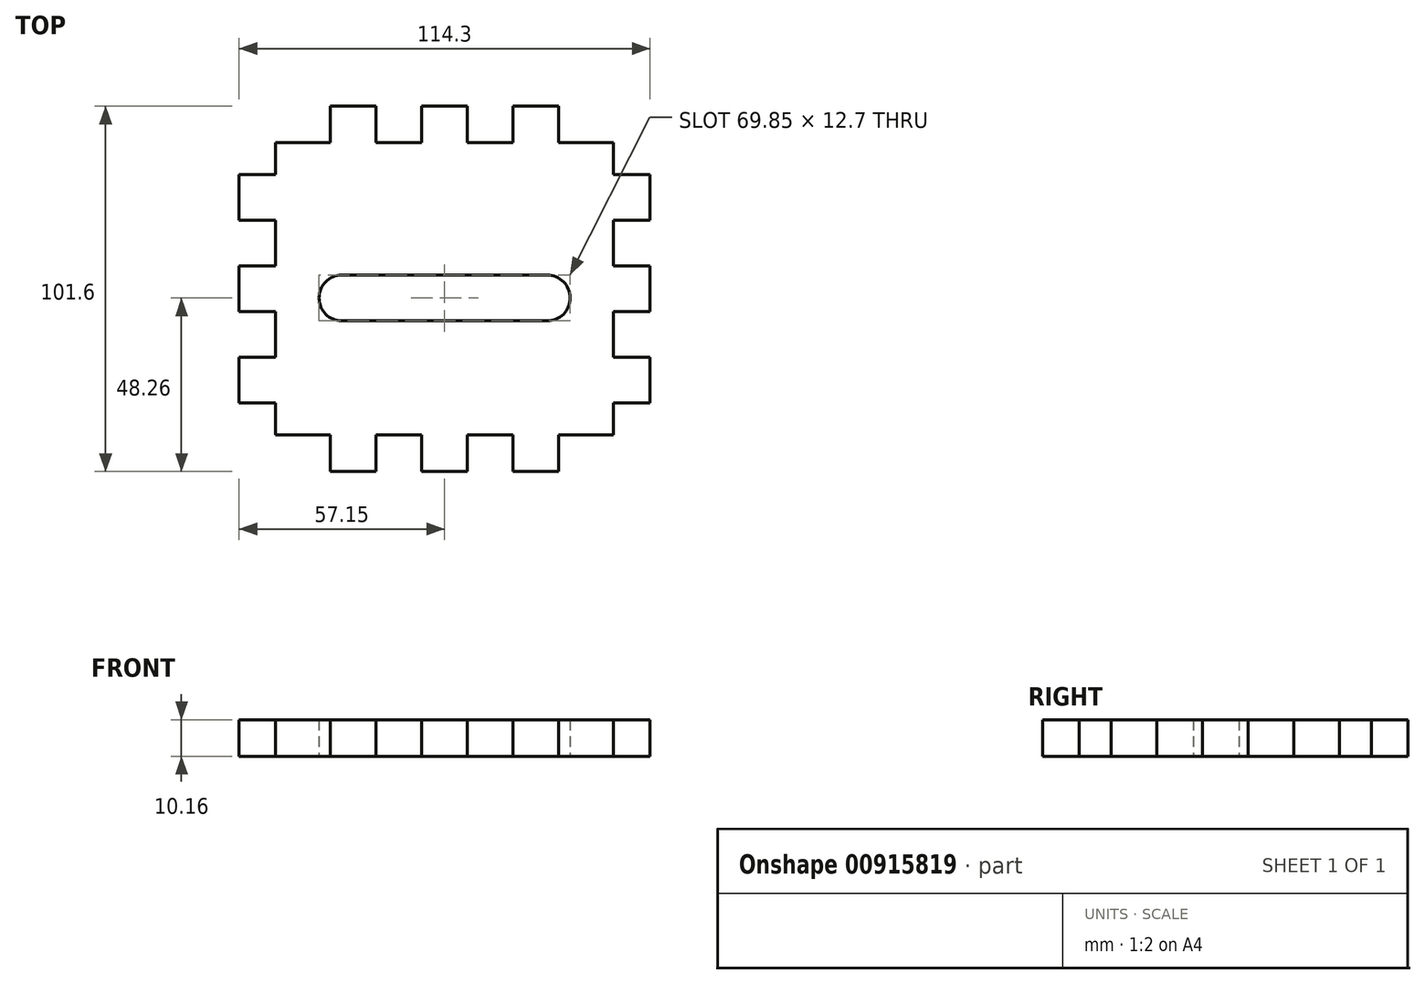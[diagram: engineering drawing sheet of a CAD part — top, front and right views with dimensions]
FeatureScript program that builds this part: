
annotation { "Feature Type Name" : "Feature", "Feature Type Description" : "" }
export const myFeature = defineFeature(function(context is Context, id is Id, definition is map)
    precondition{}
    {
        {
            var Q0;
            Q0=qCreatedBy(makeId("Top.planeOp"),FACE);
            var sketch = newSketch(context, id + "F0", { "sketchPlane" : qUnion([Q0])});
            skLineSegment(sketch, "E0.bottom", {"start": v(25.4, 0) * mm, "end": v(38.1, 0) * mm});
            skLineSegment(sketch, "E0.left", {"start": v(0, -19.05) * mm, "end": v(0, -31.75) * mm});
            skLineSegment(sketch, "E1", {"start": v(10.16, -10.16) * mm, "end": v(25.4, -10.16) * mm});
            skLineSegment(sketch, "E2", {"start": v(25.4, -10.16) * mm, "end": v(25.4, 0) * mm});
            skPoint(sketch, "E3.orphan", {"position": v(0, 0) * mm});
            skLineSegment(sketch, "E4", {"start": v(38.1, 0) * mm, "end": v(38.1, -10.16) * mm});
            skLineSegment(sketch, "E5", {"start": v(38.1, -10.16) * mm, "end": v(50.8, -10.16) * mm});
            skLineSegment(sketch, "E6", {"start": v(50.8, -10.16) * mm, "end": v(50.8, 0) * mm});
            skLineSegment(sketch, "E7", {"start": v(50.8, 0) * mm, "end": v(63.5, 0) * mm});
            skLineSegment(sketch, "E8", {"start": v(63.5, 0) * mm, "end": v(63.5, -10.16) * mm});
            skLineSegment(sketch, "E9", {"start": v(63.5, -10.16) * mm, "end": v(76.2, -10.16) * mm});
            skLineSegment(sketch, "E10", {"start": v(76.2, -10.16) * mm, "end": v(76.2, 0) * mm});
            skLineSegment(sketch, "E11.trimOffspring", {"start": v(76.2, 0) * mm, "end": v(88.9, 0) * mm});
            skLineSegment(sketch, "E12", {"start": v(88.9, 0) * mm, "end": v(88.9, -10.16) * mm});
            skLineSegment(sketch, "E13", {"start": v(88.9, -10.16) * mm, "end": v(104.14, -10.16) * mm});
            skPoint(sketch, "E14.orphan", {"position": v(114.3, 0) * mm});
            skLineSegment(sketch, "E15", {"start": v(10.16, -10.16) * mm, "end": v(10.16, -19.05) * mm});
            skLineSegment(sketch, "E16", {"start": v(10.16, -19.05) * mm, "end": v(0, -19.05) * mm});
            skLineSegment(sketch, "E17", {"start": v(0, -31.75) * mm, "end": v(10.16, -31.75) * mm});
            skLineSegment(sketch, "E18", {"start": v(10.16, -31.75) * mm, "end": v(10.16, -44.45) * mm});
            skLineSegment(sketch, "E19", {"start": v(10.16, -44.45) * mm, "end": v(0, -44.45) * mm});
            skLineSegment(sketch, "E20", {"start": v(0, -44.45) * mm, "end": v(0, -57.15) * mm});
            skLineSegment(sketch, "E21", {"start": v(0, -57.15) * mm, "end": v(10.16, -57.15) * mm});
            skLineSegment(sketch, "E22", {"start": v(10.16, -57.15) * mm, "end": v(10.16, -69.85) * mm});
            skLineSegment(sketch, "E23", {"start": v(10.16, -69.85) * mm, "end": v(0, -69.85) * mm});
            skLineSegment(sketch, "E24.trimOffspring", {"start": v(0, -69.85) * mm, "end": v(0, -82.55) * mm});
            skLineSegment(sketch, "E25", {"start": v(0, -82.55) * mm, "end": v(10.16, -82.55) * mm});
            skLineSegment(sketch, "E26", {"start": v(10.16, -82.55) * mm, "end": v(10.16, -91.44) * mm});
            skLineSegment(sketch, "E27", {"start": v(10.16, -91.44) * mm, "end": v(25.4, -91.44) * mm});
            skLineSegment(sketch, "E28", {"start": v(25.4, -91.44) * mm, "end": v(25.4, -101.6) * mm});
            skPoint(sketch, "E29.orphan", {"position": v(0, -101.6) * mm});
            skLineSegment(sketch, "E30", {"start": v(57.15, 0) * mm, "end": v(57.15, 0) * mm});
            skLineSegment(sketch, "E31", {"start": v(0, -50.8) * mm, "end": v(0, -50.8) * mm});
            skLineSegment(sketch, "E32.MirrorCS", {"start": v(104.14, -10.16) * mm, "end": v(104.14, -19.05) * mm});
            skLineSegment(sketch, "E33.MirrorCS", {"start": v(104.14, -19.05) * mm, "end": v(114.3, -19.05) * mm});
            skLineSegment(sketch, "E34.MirrorCS", {"start": v(114.3, -19.05) * mm, "end": v(114.3, -31.75) * mm});
            skLineSegment(sketch, "E35.MirrorCS", {"start": v(114.3, -31.75) * mm, "end": v(104.14, -31.75) * mm});
            skLineSegment(sketch, "E36.MirrorCS", {"start": v(104.14, -31.75) * mm, "end": v(104.14, -44.45) * mm});
            skLineSegment(sketch, "E37.MirrorCS", {"start": v(104.14, -44.45) * mm, "end": v(114.3, -44.45) * mm});
            skLineSegment(sketch, "E38.MirrorCS", {"start": v(114.3, -44.45) * mm, "end": v(114.3, -57.15) * mm});
            skLineSegment(sketch, "E39.MirrorCS", {"start": v(114.3, -57.15) * mm, "end": v(104.14, -57.15) * mm});
            skLineSegment(sketch, "E40.MirrorCS", {"start": v(104.14, -57.15) * mm, "end": v(104.14, -69.85) * mm});
            skLineSegment(sketch, "E41.MirrorCS", {"start": v(104.14, -69.85) * mm, "end": v(114.3, -69.85) * mm});
            skLineSegment(sketch, "E42.MirrorCS", {"start": v(114.3, -69.85) * mm, "end": v(114.3, -82.55) * mm});
            skLineSegment(sketch, "E43.MirrorCS", {"start": v(114.3, -82.55) * mm, "end": v(104.14, -82.55) * mm});
            skLineSegment(sketch, "E44.MirrorCS", {"start": v(104.14, -82.55) * mm, "end": v(104.14, -91.44) * mm});
            skLineSegment(sketch, "E45.MirrorCS", {"start": v(104.14, -91.44) * mm, "end": v(88.9, -91.44) * mm});
            skLineSegment(sketch, "E46.MirrorCS", {"start": v(88.9, -91.44) * mm, "end": v(88.9, -101.6) * mm});
            skLineSegment(sketch, "E47.MirrorCS", {"start": v(25.4, -101.6) * mm, "end": v(38.1, -101.6) * mm});
            skLineSegment(sketch, "E48.MirrorCS", {"start": v(38.1, -101.6) * mm, "end": v(38.1, -91.44) * mm});
            skLineSegment(sketch, "E49.MirrorCS", {"start": v(38.1, -91.44) * mm, "end": v(50.8, -91.44) * mm});
            skLineSegment(sketch, "E50.MirrorCS", {"start": v(50.8, -91.44) * mm, "end": v(50.8, -101.6) * mm});
            skLineSegment(sketch, "E51.MirrorCS", {"start": v(63.5, -101.6) * mm, "end": v(63.5, -91.44) * mm});
            skLineSegment(sketch, "E52.MirrorCS", {"start": v(63.5, -91.44) * mm, "end": v(76.2, -91.44) * mm});
            skLineSegment(sketch, "E53.MirrorCS", {"start": v(76.2, -91.44) * mm, "end": v(76.2, -101.6) * mm});
            skLineSegment(sketch, "E54.MirrorCS", {"start": v(50.8, -101.6) * mm, "end": v(63.5, -101.6) * mm});
            skLineSegment(sketch, "E55.MirrorCS", {"start": v(76.2, -101.6) * mm, "end": v(88.9, -101.6) * mm});
            skLineSegment(sketch, "E56.bottom", {"start": v(28.57, -47) * mm, "end": v(85.72, -47) * mm});
            skLineSegment(sketch, "E56.top", {"start": v(28.57, -59.7) * mm, "end": v(85.72, -59.7) * mm});
            skLineSegment(sketch, "E56.left", {"start": v(22.22, -53.34) * mm, "end": v(22.22, -53.34) * mm});
            skLineSegment(sketch, "E56.right", {"start": v(92.07, -53.34) * mm, "end": v(92.07, -53.34) * mm});
            skPoint(sketch, "E57.visualSharp", {"position": v(22.22, -47) * mm});
            skArc(sketch, "E57.filletArc", {"start": v(28.57, -47) * mm, "mid": v(24.08, -48.85) * mm, "end": v(22.22, -53.34) * mm});
            skPoint(sketch, "E58.visualSharp", {"position": v(22.22, -59.7) * mm});
            skArc(sketch, "E58.filletArc", {"start": v(22.22, -53.34) * mm, "mid": v(24.08, -57.83) * mm, "end": v(28.57, -59.7) * mm});
            skPoint(sketch, "E59.visualSharp", {"position": v(92.08, -47) * mm});
            skArc(sketch, "E59.filletArc", {"start": v(92.07, -53.34) * mm, "mid": v(90.22, -48.85) * mm, "end": v(85.72, -47) * mm});
            skPoint(sketch, "E60.visualSharp", {"position": v(92.07, -59.7) * mm});
            skArc(sketch, "E60.filletArc", {"start": v(85.72, -59.7) * mm, "mid": v(90.22, -57.83) * mm, "end": v(92.07, -53.34) * mm});
            skLineSegment(sketch, "E61", {"start": v(57.15, 0) * mm, "end": v(57.15, -47) * mm, "construction": true});
            skSolve(sketch);
        }
        {
            var Q0;
            Q0=makeQuery(id+"F0.imprint","IMPRINT",FACE,{"disambiguationData":[TD([[makeQuery(id+"F0.imprint","IMPRINT",EDGE,{"derivedFrom":sQuery(id+"F0.wireOp",EDGE,"E1")}),-1.0]])]});
            extrude(context, id + "F1", {"entities" : qUnion([Q0]), "depth" : 10.16 * mm, "offsetDistance" : 25.4 * mm});
        }
    });
